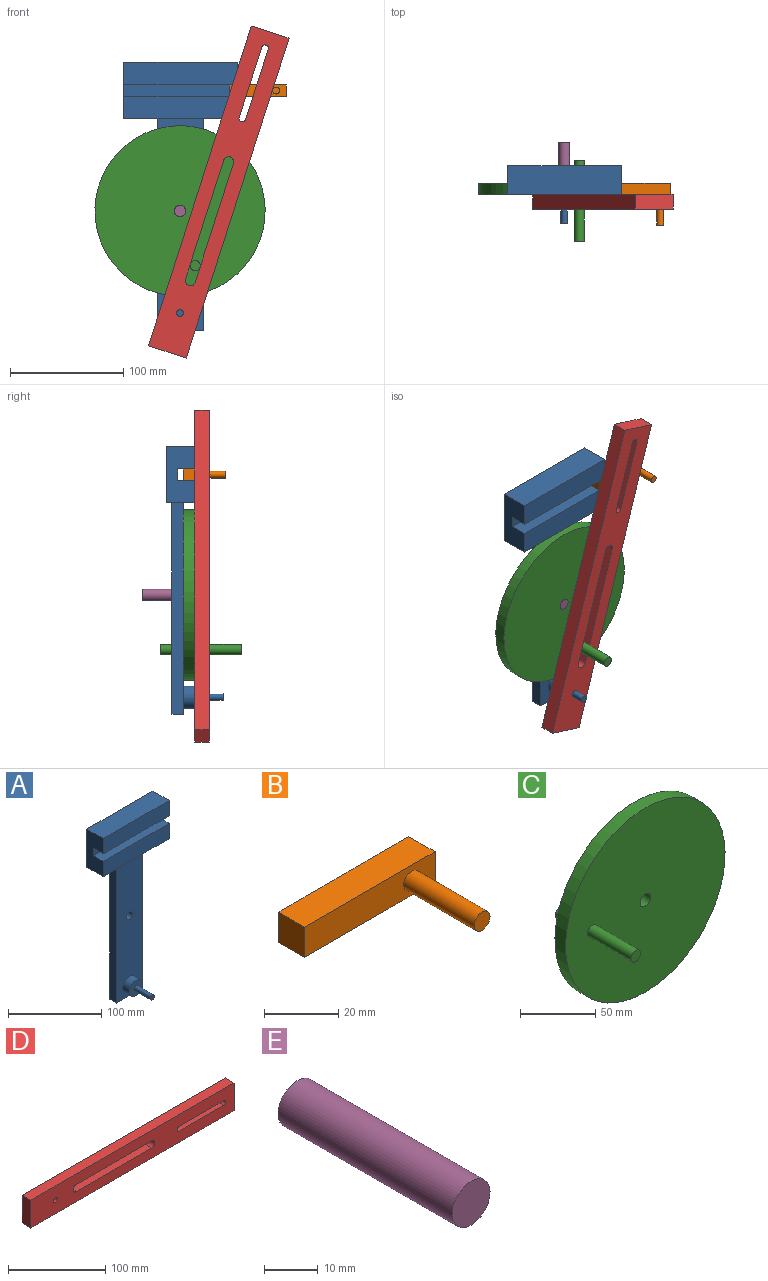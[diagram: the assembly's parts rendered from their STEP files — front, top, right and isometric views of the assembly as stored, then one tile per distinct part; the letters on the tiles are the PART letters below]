
ASSEMBLY  parts=5 mates=6
PART A: 20 faces, bbox 100x50x236 mm
  f0: plane 186x40mm, normal (0,1,0), area 7361.5mm2, adj f1,f12,f13,f14,f19
  f1: plane 100x25mm, normal (0,0,-1), area 2100mm2, adj f0,f2,f8,f9,f10,f11,f12,f13
  f2: plane 100x50mm, normal (0,1,0), area 5000mm2, adj f1,f3,f9,f10
  f3: plane 100x25mm, normal (0,0,1), area 2500mm2, adj f2,f4,f9,f10
  f4: plane 100x20mm, normal (0,-1,0), area 2000mm2, adj f3,f5,f9,f10
  f5: plane 100x15mm, normal (0,0,-1), area 1500mm2, adj f4,f6,f9,f10
  f6: plane 100x10mm, normal (0,-1,0), area 1000mm2, adj f5,f7,f9,f10
  f7: plane 100x15mm, normal (0,0,1), area 1500mm2, adj f6,f8,f9,f10
  f8: plane 100x20mm, normal (0,-1,0), area 2000mm2, adj f1,f7,f9,f10
  f9: plane 50x25mm, normal (-1,0,0), area 1100mm2, adj f1,f2,f3,f4,f5,f6,f7,f8
  f10: plane 50x25mm, normal (1,0,0), area 1100mm2, adj f1,f2,f3,f4,f5,f6,f7,f8
  f11: plane 186x40mm, normal (0,-1,0), area 7047.3mm2, adj f1,f12,f13,f14,f16,f19
  f12: plane 186x10mm, normal (-1,0,0), area 1860mm2, adj f0,f1,f11,f14
  f13: plane 186x10mm, normal (1,0,0), area 1860mm2, adj f0,f1,f11,f14
  f14: plane 40x10mm, normal (0,0,-1), area 400mm2, adj f0,f11,f12,f13
  f15: plane 20x20mm, normal (0,-1,0), area 285.9mm2, adj f16,f18
  f16: cylinder r=10mm len=20mm, axis (0,1,0), area 628.3mm2, adj f11,f15
  f17: plane 6x6mm, normal (0,-1,0), area 28.3mm2, adj f18
  f18: cylinder r=3mm len=25mm, axis (0,1,0), area 471.2mm2, adj f15,f17
  f19: cylinder r=5mm len=10mm, axis (0,1,0), area 314.2mm2, adj f0,f11
PART B: 8 faces, bbox 50x37x10 mm
  f0: plane 50x9.96mm, normal (0,1,0), area 498mm2, adj f1,f3,f4,f5
  f1: plane 50x10mm, normal (0,0,1), area 500mm2, adj f0,f2,f4,f5
  f2: plane 50x9.96mm, normal (0,-1,0), area 469.7mm2, adj f1,f3,f4,f5,f6
  f3: plane 50x10mm, normal (0,0,-1), area 500mm2, adj f0,f2,f4,f5
  f4: plane 10x9.96mm, normal (1,0,0), area 99.6mm2, adj f0,f1,f2,f3
  f5: plane 10x9.96mm, normal (-1,0,0), area 99.6mm2, adj f0,f1,f2,f3
  f6: cylinder r=3mm len=27mm, axis (0,1,0), area 508.9mm2, adj f2,f7
  f7: plane 6x6mm, normal (0,-1,0), area 28.3mm2, adj f6
PART C: 8 faces, bbox 150x71x150 mm
  f0: cylinder r=5mm len=10mm, axis (0,1,0), area 314.2mm2, adj f2,f3
  f1: cylinder r=75mm len=150mm, axis (0,1,0), area 4712.4mm2, adj f2,f3
  f2: plane 150x150mm, normal (0,-1,0), area 17529.3mm2, adj f0,f1,f6
  f3: plane 150x150mm, normal (0,1,0), area 17529.3mm2, adj f0,f1,f5
  f4: plane 9x9mm, normal (0,1,0), area 63.6mm2, adj f5
  f5: cylinder r=4.5mm len=20mm, axis (0,1,0), area 565.5mm2, adj f3,f4
  f6: cylinder r=4.5mm len=41mm, axis (0,1,0), area 1159.2mm2, adj f2,f7
  f7: plane 9x9mm, normal (0,-1,0), area 63.6mm2, adj f6
PART D: 15 faces, bbox 296x13x35 mm
  f0: cylinder r=4.5mm len=13mm, axis (0,1,0), area 183.8mm2, adj f1,f12,f13,f14
  f1: plane 110x13mm, normal (0,0,-1), area 1430mm2, adj f0,f2,f13,f14
  f2: cylinder r=4.5mm len=13mm, axis (0,1,0), area 183.8mm2, adj f1,f12,f13,f14
  f3: cylinder r=3mm len=13mm, axis (0,1,0), area 122.5mm2, adj f4,f9,f13,f14
  f4: plane 65x13mm, normal (0,0,-1), area 845mm2, adj f3,f5,f13,f14
  f5: cylinder r=3mm len=13mm, axis (0,1,0), area 122.5mm2, adj f4,f9,f13,f14
  f6: plane 35x13mm, normal (1,0,0), area 455mm2, adj f7,f10,f13,f14
  f7: plane 296x13mm, normal (0,0,1), area 3848mm2, adj f6,f8,f13,f14
  f8: plane 35x13mm, normal (-1,0,0), area 455mm2, adj f7,f10,f13,f14
  f9: plane 65x13mm, normal (0,0,1), area 845mm2, adj f3,f5,f13,f14
  f10: plane 296x13mm, normal (0,0,-1), area 3848mm2, adj f6,f8,f13,f14
  f11: cylinder r=3mm len=13mm, axis (0,1,0), area 245mm2, adj f13,f14
  f12: plane 110x13mm, normal (0,0,1), area 1430mm2, adj f0,f2,f13,f14
  f13: plane 296x35mm, normal (0,-1,0), area 8859.8mm2, adj f0,f1,f2,f3,f4,f5,f6,f7
  f14: plane 296x35mm, normal (0,1,0), area 8859.8mm2, adj f0,f1,f2,f3,f4,f5,f6,f7
PART E: 3 faces, bbox 10x45.7x10 mm
  f0: cylinder r=4.98mm len=45.7mm, axis (0,1,0), area 1430mm2, adj f1,f2
  f1: plane 9.96x9.96mm, normal (0,-1,0), area 77.9mm2, adj f0
  f2: plane 9.96x9.96mm, normal (0,1,0), area 77.9mm2, adj f0
PLACE A t=(34.74,20.03,6.33)mm fixed
PLACE B rot(axis=(0,1,-0.01),0deg) t=(27.92,15.03,6.31)mm
PLACE C rot(axis=(0,-1,0),105.5deg) t=(-107.33,25.03,-47.72)mm
PLACE D rot(axis=(0,-1,0),72.2deg) t=(-69.34,-4.97,-185.3)mm
PLACE E rot(axis=(0.84,0,0.55),180deg) t=(78.6,-9.97,-60.26)mm
MATE revolute E.f0 <-> C.f0  axis (0,-1,0) through (-15.76,-4.97,-74.67)mm
MATE pin_slot C.f5 <-> D.f14  axis (0,1,0) through (-2.36,-4.97,-122.84)mm
MATE revolute D.f11 <-> A.f16  axis (0,1,0) through (-15.77,-4.97,-164.67)mm
MATE revolute A.f19 <-> C.f0  axis (0,-1,0) through (-15.76,5.03,-74.67)mm
MATE slider B.f4 <-> A.f10  axis (1,0,0) through (77.92,-4.97,26.33)mm
MATE pin_slot B.f6 <-> D.f14  axis (0,1,0) through (68.92,-4.97,31.33)mm
